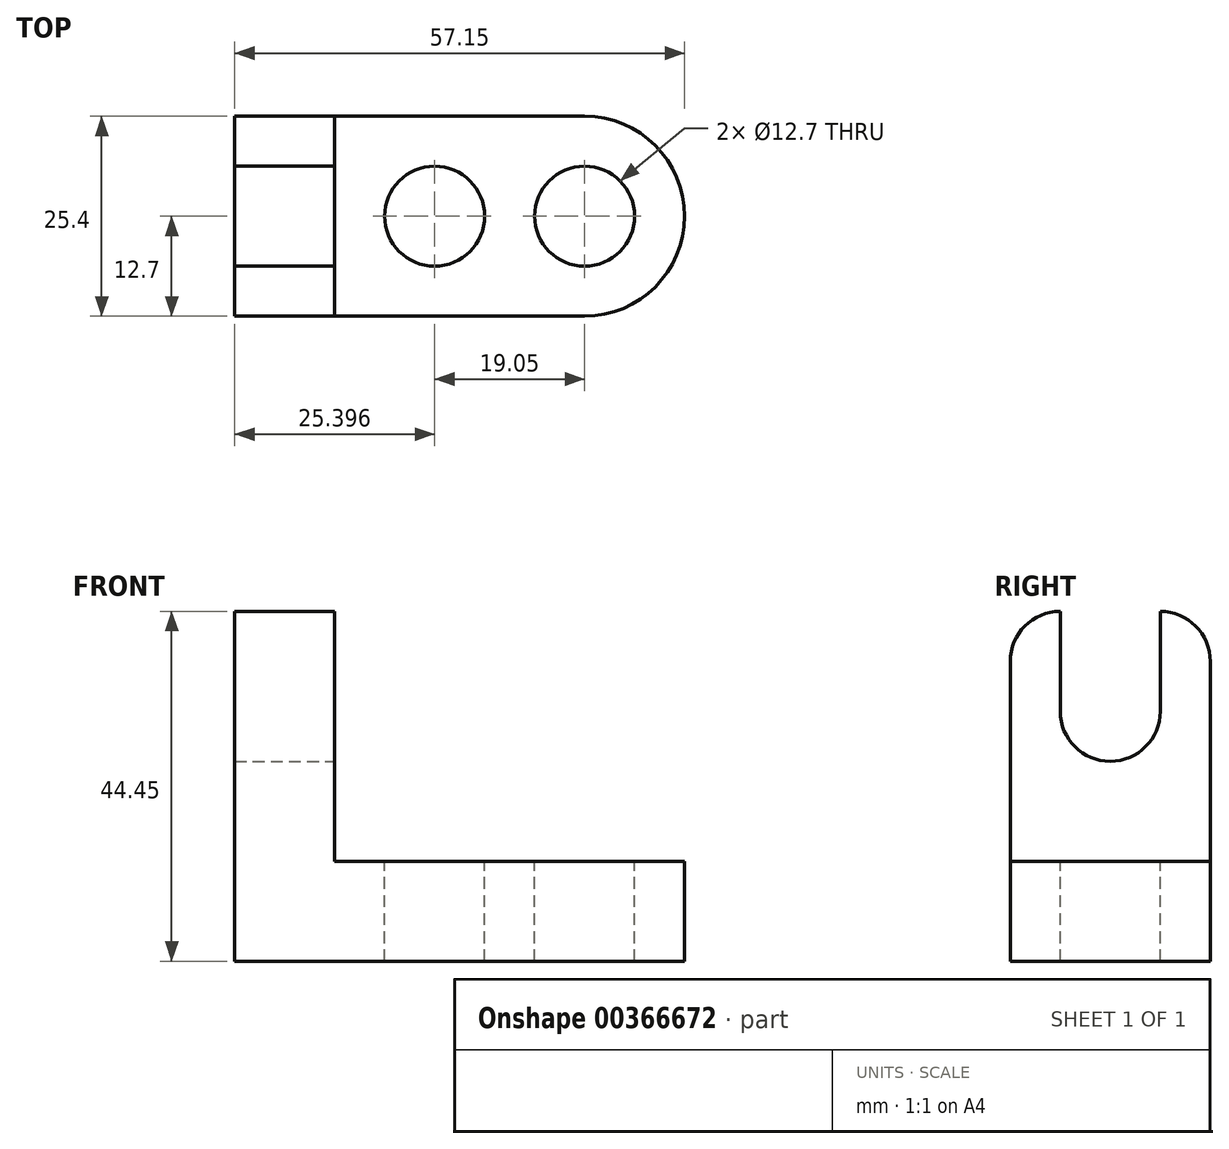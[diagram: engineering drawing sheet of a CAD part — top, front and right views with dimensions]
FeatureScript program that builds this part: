
annotation { "Feature Type Name" : "Feature", "Feature Type Description" : "" }
export const myFeature = defineFeature(function(context is Context, id is Id, definition is map)
    precondition{}
    {
        {
            var Q0;
            Q0=qCreatedBy(makeId("Front.planeOp"),FACE);
            var sketch = newSketch(context, id + "F0", { "sketchPlane" : qUnion([Q0])});
            skLineSegment(sketch, "E0", {"start": v(-65.93, 0) * mm, "end": v(-65.93, 44.45) * mm});
            skLineSegment(sketch, "E1", {"start": v(-65.93, 44.45) * mm, "end": v(-8.78, 44.45) * mm});
            skLineSegment(sketch, "E2", {"start": v(-8.78, 44.45) * mm, "end": v(-8.78, 0) * mm});
            skLineSegment(sketch, "E3", {"start": v(-8.78, 0) * mm, "end": v(-65.93, 0) * mm});
            skSolve(sketch);
        }
        {
            var Q0;
            Q0=makeQuery(id+"F0.imprint","IMPRINT",FACE,{"disambiguationData":[TD([[makeQuery(id+"F0.imprint","IMPRINT",EDGE,{"derivedFrom":sQuery(id+"F0.wireOp",EDGE,"E0")}),-1.0]])]});
            extrude(context, id + "F1", {"entities" : qUnion([Q0]), "depth" : 25.4 * mm});
        }
        {
            var Q0;
            Q0=makeQuery(id+"F1.opExtrude","CAP_FACE",FACE,{"disambiguationData":[OSD([sQuery(id+"F0.wireOp",EDGE,"E0"),sQuery(id+"F0.wireOp",EDGE,"E1"),sQuery(id+"F0.wireOp",EDGE,"E2"),sQuery(id+"F0.wireOp",EDGE,"E3")])],"isStart":false});
            var sketch = newSketch(context, id + "F2", { "sketchPlane" : qUnion([Q0])});
            skLineSegment(sketch, "E4", {"start": v(-53.23, 44.45) * mm, "end": v(-53.23, 12.7) * mm});
            skLineSegment(sketch, "E5", {"start": v(-53.23, 12.7) * mm, "end": v(-8.78, 12.7) * mm});
            skSolve(sketch);
        }
        {
            var Q0;
            {var subQ0=sQuery(id+"F2.wireOp",EDGE,"E4");Q0=makeQuery(id+"F2.imprint","IMPRINT",FACE,{"disambiguationData":[TD([[makeQuery(id+"F2.imprint","IMPRINT",EDGE,{"derivedFrom":subQ0}),1.0]])]});}
            extrude(context, id + "F3", {"entities" : qUnion([Q0]), "operationType" : NewBodyOperationType.REMOVE, "oppositeDirection" : true, "depth" : 25.4 * mm});
        }
        {
            var Q0;
            Q0=makeQuery(id+"F3.boolean.opBoolean","COPY",FACE,{"derivedFrom":makeQuery(id+"F3.opExtrude","SWEPT_FACE",FACE,{"disambiguationData":[OSD([sQuery(id+"F2.wireOp",EDGE,"E5")])]})});
            var sketch = newSketch(context, id + "F4", { "sketchPlane" : qUnion([Q0])});
            skCircle(sketch, "E6", {"center": v(-40.53, -12.7) * mm, "radius": 6.35 * mm});
            skCircle(sketch, "E7", {"center": v(-21.48, -12.7) * mm, "radius": 6.35 * mm});
            skArc(sketch, "E8", {"start": v(-21.48, -25.4) * mm, "mid": v(-8.78, -12.7) * mm, "end": v(-21.48, 0) * mm});
            skSolve(sketch);
        }
        {
            var Q0;
            Q0=makeQuery(id+"F4.imprint","IMPRINT",FACE,{"disambiguationData":[TD([[makeQuery(id+"F4.imprint","IMPRINT",EDGE,{"derivedFrom":sQuery(id+"F4.wireOp",EDGE,"E7")}),1.0]])]});
            var Q1;
            Q1=makeQuery(id+"F4.imprint","IMPRINT",FACE,{"disambiguationData":[TD([[makeQuery(id+"F4.imprint","IMPRINT",EDGE,{"derivedFrom":sQuery(id+"F4.wireOp",EDGE,"E6")}),1.0]])]});
            var Q2;
            {var subQ0=sQuery(id+"F4.wireOp",EDGE,"E8");var subQ1=sQuery(id+"F2.wireOp",EDGE,"E5");var subQ2=makeQuery(id+"F3.boolean.opBoolean","COPY",EDGE,{"derivedFrom":makeQuery(id+"F3.opExtrude","CAP_EDGE",EDGE,{"disambiguationData":[OSD([subQ1])],"isStart":true})});var subQ3=makeQuery(id+"F4.imprint","INTERSECT",VERTEX,{"derivedFrom":[subQ2,subQ0]});Q2=makeQuery(id+"F4.imprint","IMPRINT",FACE,{"disambiguationData":[TD([[makeQuery(id+"F4.imprint","IMPRINT",EDGE,{"disambiguationData":[TD([[subQ3,-1.0]])],"derivedFrom":subQ0}),-1.0]])]});}
            var Q3;
            {var subQ0=sQuery(id+"F4.wireOp",EDGE,"E8");var subQ1=sQuery(id+"F2.wireOp",EDGE,"E5");var subQ2=makeQuery(id+"F3.boolean.opBoolean","COPY",EDGE,{"derivedFrom":makeQuery(id+"F3.opExtrude","CAP_EDGE",EDGE,{"disambiguationData":[OSD([subQ1])],"isStart":false})});var subQ3=makeQuery(id+"F4.imprint","INTERSECT",VERTEX,{"derivedFrom":[subQ2,subQ0]});Q3=makeQuery(id+"F4.imprint","IMPRINT",FACE,{"disambiguationData":[TD([[makeQuery(id+"F4.imprint","IMPRINT",EDGE,{"disambiguationData":[TD([[subQ3,1.0]])],"derivedFrom":subQ0}),-1.0]])]});}
            extrude(context, id + "F5", {"entities" : qUnion([Q0, Q1, Q2, Q3]), "operationType" : NewBodyOperationType.REMOVE, "oppositeDirection" : true, "depth" : 25.4 * mm});
        }
        {
            var Q0;
            Q0=makeQuery(id+"F3.boolean.opBoolean","COPY",FACE,{"derivedFrom":makeQuery(id+"F3.opExtrude","SWEPT_FACE",FACE,{"disambiguationData":[OSD([sQuery(id+"F2.wireOp",EDGE,"E4")])]})});
            var sketch = newSketch(context, id + "F6", { "sketchPlane" : qUnion([Q0])});
            skCircle(sketch, "E9", {"center": v(-12.7, 31.75) * mm, "radius": 6.35 * mm});
            skLineSegment(sketch, "E10", {"start": v(-19.05, 31.75) * mm, "end": v(-19.05, 44.45) * mm});
            skPoint(sketch, "E10.endSnap0", {"position": v(-12.7, 44.45) * mm});
            skLineSegment(sketch, "E11", {"start": v(-6.35, 31.75) * mm, "end": v(-6.35, 44.45) * mm});
            skArc(sketch, "E12", {"start": v(-19.05, 44.45) * mm, "mid": v(-23.54, 42.6) * mm, "end": v(-25.4, 38.1) * mm});
            skArc(sketch, "E13", {"start": v(0, 38.1) * mm, "mid": v(-1.86, 42.6) * mm, "end": v(-6.35, 44.45) * mm});
            skSolve(sketch);
        }
        {
            var Q0;
            {var subQ0=sQuery(id+"F6.wireOp",EDGE,"E12");Q0=makeQuery(id+"F6.imprint","IMPRINT",FACE,{"disambiguationData":[TD([[makeQuery(id+"F6.imprint","IMPRINT",EDGE,{"derivedFrom":subQ0}),-1.0]])]});}
            var Q1;
            {var subQ0=sQuery(id+"F6.wireOp",EDGE,"E10");Q1=makeQuery(id+"F6.imprint","IMPRINT",FACE,{"disambiguationData":[TD([[makeQuery(id+"F6.imprint","IMPRINT",EDGE,{"derivedFrom":subQ0}),-1.0]])]});}
            var Q2;
            {var subQ0=sQuery(id+"F6.wireOp",EDGE,"E9");var subQ1=makeQuery(id+"F6.imprint","INTERSECT",VERTEX,{"derivedFrom":[subQ0,sQuery(id+"F6.wireOp",EDGE,"E10")]});Q2=makeQuery(id+"F6.imprint","IMPRINT",FACE,{"disambiguationData":[TD([[makeQuery(id+"F6.imprint","IMPRINT",EDGE,{"disambiguationData":[TD([[subQ1,1.0]])],"derivedFrom":subQ0}),1.0]])]});}
            var Q3;
            {var subQ0=sQuery(id+"F6.wireOp",EDGE,"E13");Q3=makeQuery(id+"F6.imprint","IMPRINT",FACE,{"disambiguationData":[TD([[makeQuery(id+"F6.imprint","IMPRINT",EDGE,{"derivedFrom":subQ0}),-1.0]])]});}
            extrude(context, id + "F7", {"entities" : qUnion([Q0, Q1, Q2, Q3]), "operationType" : NewBodyOperationType.REMOVE, "oppositeDirection" : true, "depth" : 25.4 * mm});
        }
    });
